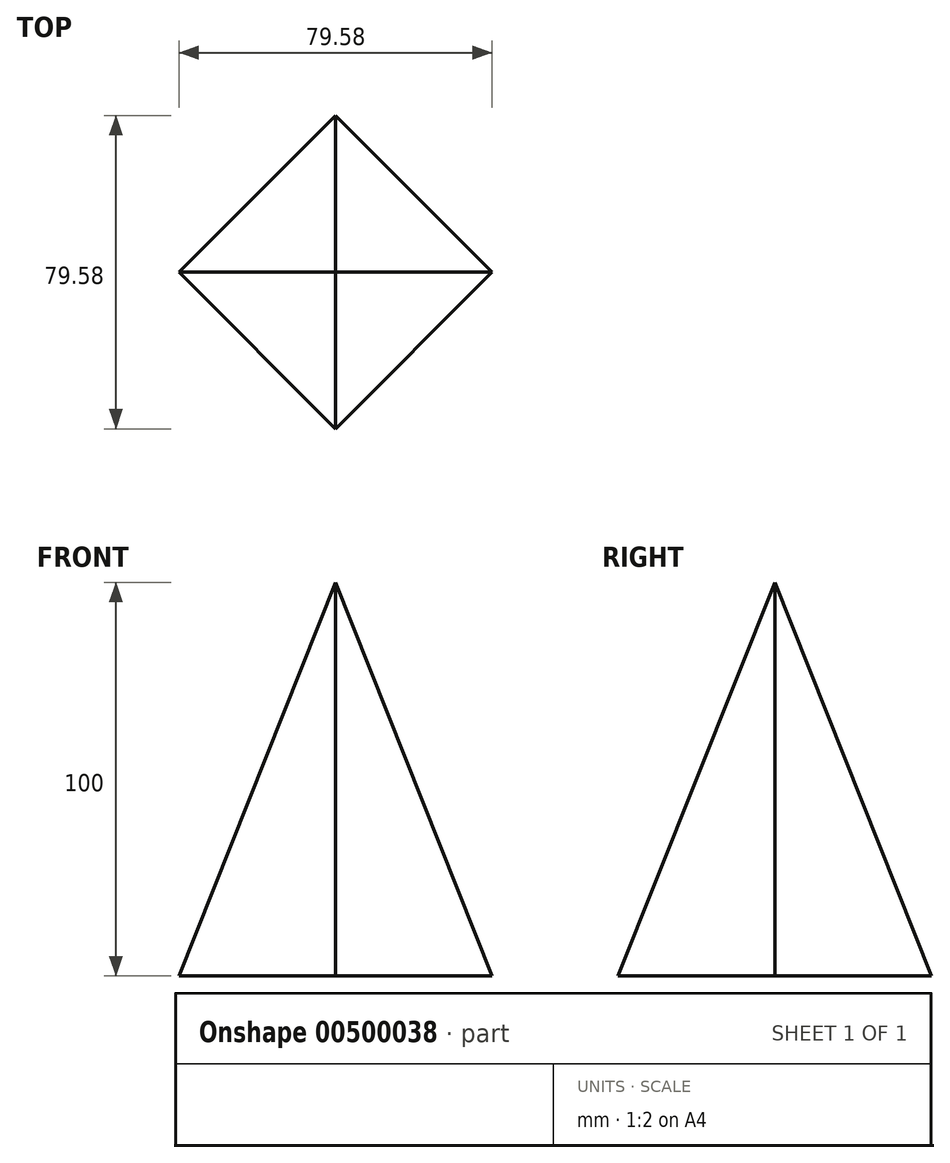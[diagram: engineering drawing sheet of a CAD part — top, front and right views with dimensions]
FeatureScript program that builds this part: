
annotation { "Feature Type Name" : "Feature", "Feature Type Description" : "" }
export const myFeature = defineFeature(function(context is Context, id is Id, definition is map)
    precondition{}
    {
        {
            var Q0;
            Q0=qCreatedBy(makeId("Top.planeOp"),FACE);
            var sketch = newSketch(context, id + "F0", { "sketchPlane" : qUnion([Q0])});
            skCircle(sketch, "E0.cCircle", {"center": v(0, 0) * mm, "radius": 39.79 * mm, "construction": true});
            skLineSegment(sketch, "E0.0", {"start": v(39.79, 0) * mm, "end": v(0, -39.79) * mm});
            skLineSegment(sketch, "E0.1", {"start": v(0, -39.79) * mm, "end": v(-39.79, 0) * mm});
            skLineSegment(sketch, "E0.2", {"start": v(-39.79, 0) * mm, "end": v(0, 39.79) * mm});
            skLineSegment(sketch, "E0.3", {"start": v(0, 39.79) * mm, "end": v(39.79, 0) * mm});
            skSolve(sketch);
        }
        {
            var Q0;
            Q0=qCreatedBy(makeId("Top.planeOp"),FACE);
            cPlane(context, id + "F1", {"entities" : qUnion([Q0]), "cplaneType" : CPlaneType.OFFSET, "offset" : 100 * mm, "width" : 152.4 * mm, "height" : 152.4 * mm});
        }
        {
            var Q0;
            Q0=qCreatedBy(id+"F1.planeOp",FACE);
            var sketch = newSketch(context, id + "F2", { "sketchPlane" : qUnion([Q0])});
            skPoint(sketch, "E1", {"position": v(0, 0) * mm});
            skSolve(sketch);
        }
        {
            var Q0;
            Q0=makeQuery(id+"F0.imprint","IMPRINT",FACE,{"disambiguationData":[TD([[makeQuery(id+"F0.imprint","IMPRINT",EDGE,{"derivedFrom":sQuery(id+"F0.wireOp",EDGE,"E0.0")}),-1.0]])]});
            var Q1;
            Q1=sQuery(id+"F2.wireOp",VERTEX,"E1");
            loft(context, id + "F3", {"sheetProfilesArray" : [{ "sheetProfileEntities" : qUnion([Q0]) }, { "sheetProfileEntities" : qUnion([Q1]) }]});
        }
    });
